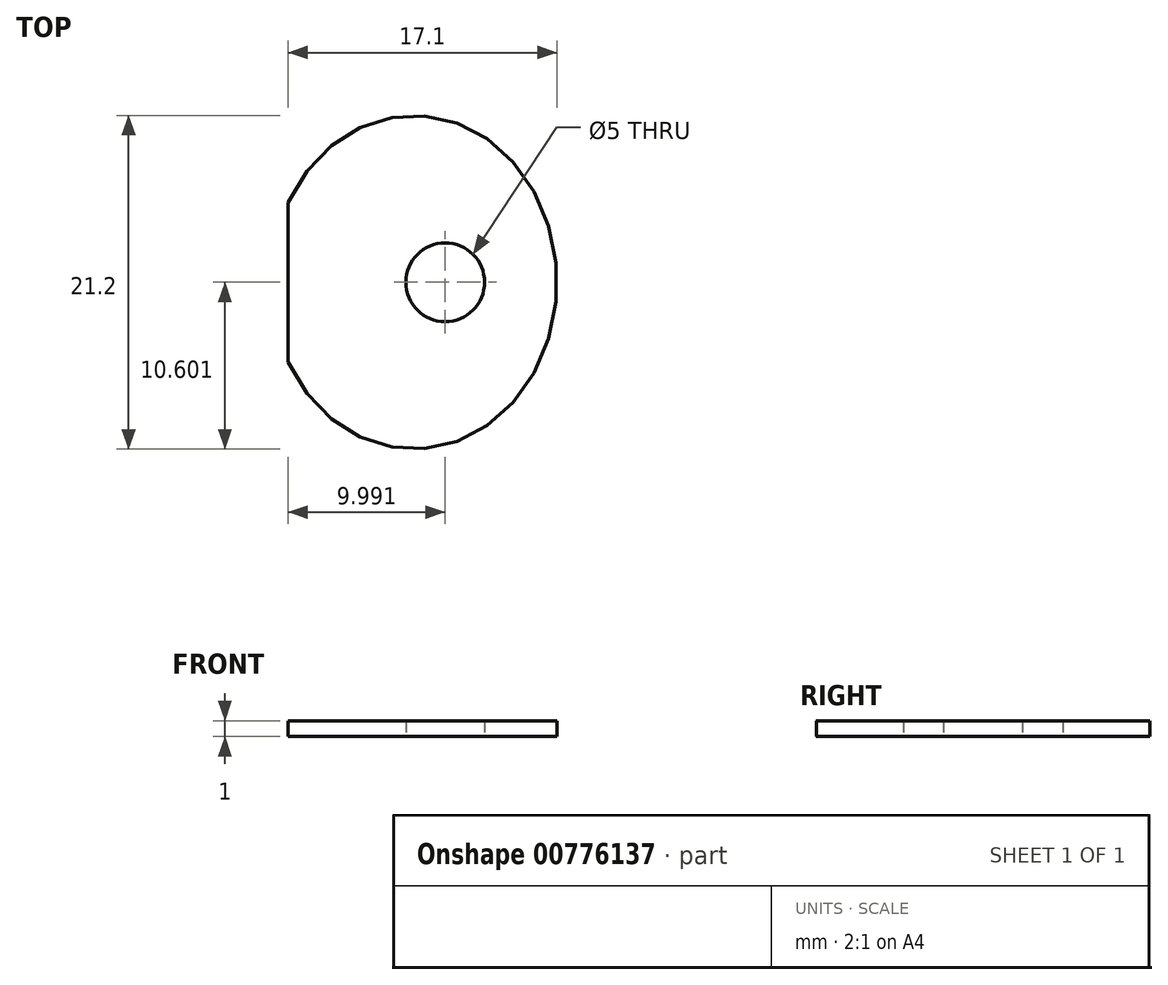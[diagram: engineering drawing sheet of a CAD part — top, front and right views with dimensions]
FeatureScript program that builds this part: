
annotation { "Feature Type Name" : "Feature", "Feature Type Description" : "" }
export const myFeature = defineFeature(function(context is Context, id is Id, definition is map)
    precondition{}
    {
        {
            var Q0;
            Q0=qCreatedBy(makeId("Top.planeOp"),FACE);
            var sketch = newSketch(context, id + "F0", { "sketchPlane" : qUnion([Q0])});
            skEllipticalArc(sketch, "E0", {});
            skLineSegment(sketch, "E1", {"start": v(10.22, 0.31) * mm, "end": v(3.17, 0.31) * mm});
            skLineSegment(sketch, "E2", {"start": v(-4.83, 0.33) * mm, "end": v(-4.83, 5.37) * mm});
            skLineSegment(sketch, "E3.MirrorCS", {"start": v(-4.83, 0.29) * mm, "end": v(-4.83, -4.75) * mm});
            skPoint(sketch, "E4.orphan", {"position": v(-4.83, 8.4) * mm});
            skPoint(sketch, "E5.orphan", {"position": v(-4.83, -7.79) * mm});
            skPoint(sketch, "E6.orphan", {"position": v(-5.93, 0.31) * mm});
            skLineSegment(sketch, "E7", {"start": v(10.22, 0.31) * mm, "end": v(3.22, 0.31) * mm, "construction": true});
            skLineSegment(sketch, "E8", {"start": v(10.22, 0.31) * mm, "end": v(7.22, 0.31) * mm, "construction": true});
            skCircle(sketch, "E9", {"center": v(5.16, 0.31) * mm, "radius": 2.5 * mm});
            skPoint(sketch, "E10.end.orphan", {"position": v(3.17, 8.86) * mm});
            skPoint(sketch, "E10.start.orphan", {"position": v(3.17, 10.91) * mm});
            skLineSegment(sketch, "E11", {"start": v(-4.83, 5.37) * mm, "end": v(-4.83, -4.75) * mm});
            const initialGuessF0  = {"E0": [0.003168321265839074, 0.0003110917252862435, 0, 1, 0.0106, 0.0091, 2.0686928027733273, 1.0728998508164656]};
            skSetInitialGuess(sketch, initialGuessF0);
            skSolve(sketch);
        }
        {
            var Q0;
            {var subQ0=sQuery(id+"F0.wireOp",EDGE,"E0");Q0=makeQuery(id+"F0.imprint","IMPRINT",FACE,{"disambiguationData":[TD([[makeQuery(id+"F0.imprint","IMPRINT",EDGE,{"derivedFrom":subQ0}),1.0]])]});}
            extrude(context, id + "F1", {"entities" : qUnion([Q0]), "depth" : 1 * mm, "offsetDistance" : 25 * mm});
        }
    });
